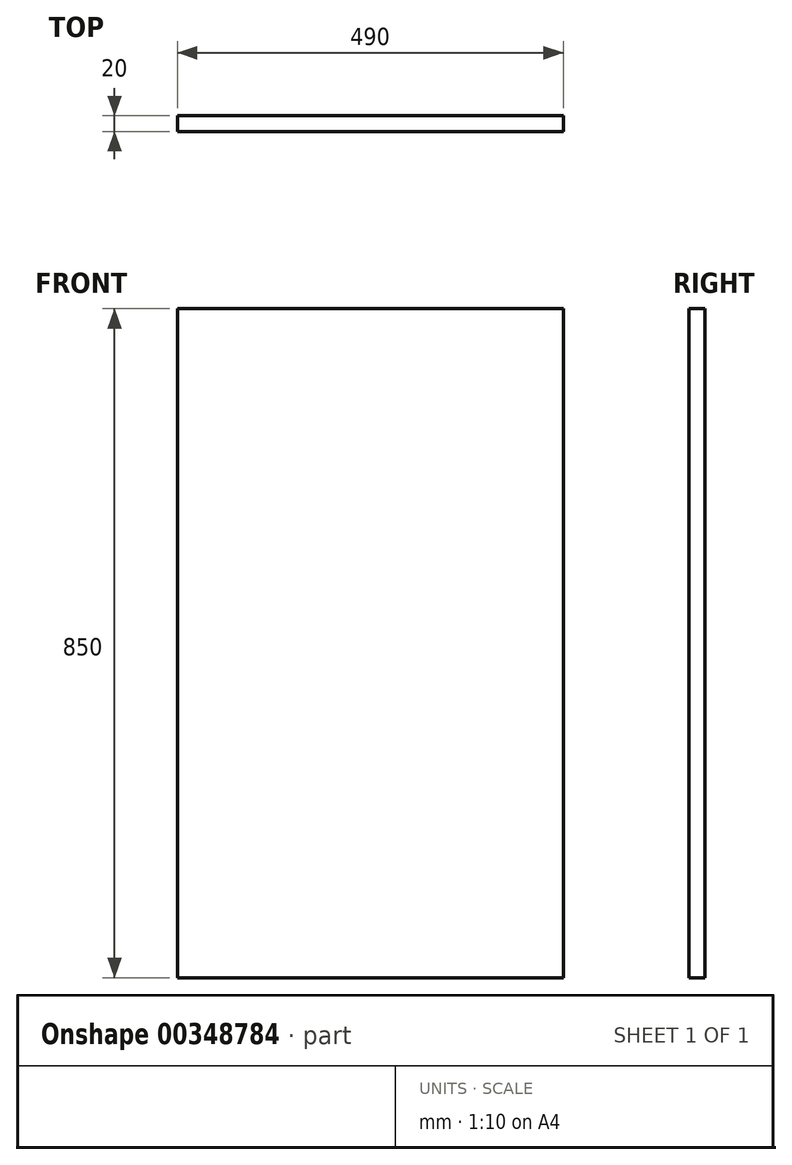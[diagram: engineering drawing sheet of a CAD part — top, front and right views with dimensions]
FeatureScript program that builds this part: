
annotation { "Feature Type Name" : "Feature", "Feature Type Description" : "" }
export const myFeature = defineFeature(function(context is Context, id is Id, definition is map)
    precondition{}
    {
        {
            var Q0;
            Q0=qCreatedBy(makeId("Front.planeOp"),FACE);
            var sketch = newSketch(context, id + "F0", { "sketchPlane" : qUnion([Q0])});
            skLineSegment(sketch, "E0.bottom", {"start": v(-490, -850) * mm, "end": v(0, -850) * mm});
            skLineSegment(sketch, "E0.top", {"start": v(-490, 0) * mm, "end": v(0, 0) * mm});
            skLineSegment(sketch, "E0.left", {"start": v(-490, -850) * mm, "end": v(-490, 0) * mm});
            skLineSegment(sketch, "E0.right", {"start": v(0, -850) * mm, "end": v(0, 0) * mm});
            skSolve(sketch);
        }
        {
            var Q0;
            Q0=qSketchRegion(id+"F0",true);
            extrude(context, id + "F1", {"entities" : qUnion([Q0]), "depth" : 20 * mm});
        }
    });
